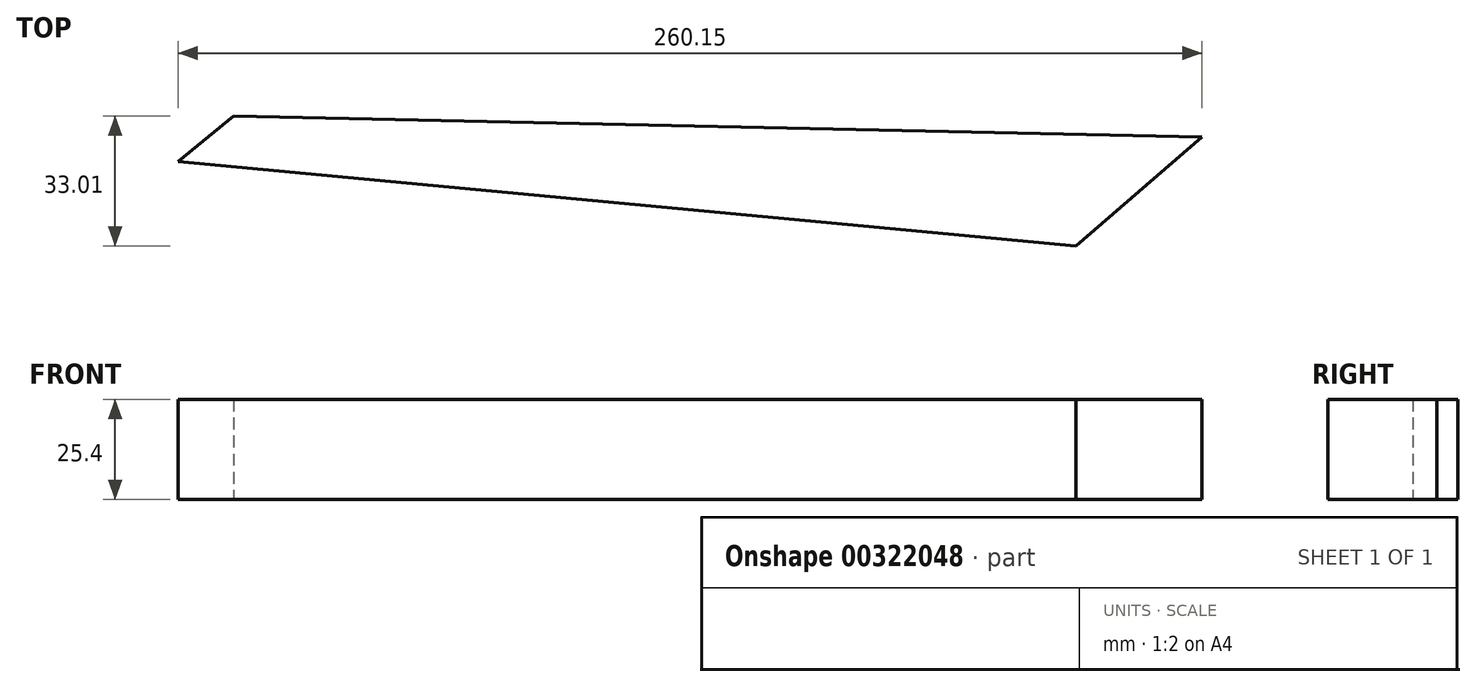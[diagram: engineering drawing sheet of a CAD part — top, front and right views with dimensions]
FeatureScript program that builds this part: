
annotation { "Feature Type Name" : "Feature", "Feature Type Description" : "" }
export const myFeature = defineFeature(function(context is Context, id is Id, definition is map)
    precondition{}
    {
        {
            var Q0;
            Q0=qCreatedBy(makeId("Top.planeOp"),FACE);
            var sketch = newSketch(context, id + "F0", { "sketchPlane" : qUnion([Q0])});
            skLineSegment(sketch, "E0", {"start": v(91.5, -86.95) * mm, "end": v(-136.55, -65.48) * mm});
            skLineSegment(sketch, "E1", {"start": v(-137.64, -66.37) * mm, "end": v(-122.43, -53.94) * mm});
            skLineSegment(sketch, "E2", {"start": v(-122.43, -53.94) * mm, "end": v(123.6, -59.33) * mm});
            skLineSegment(sketch, "E3", {"start": v(123.6, -59.33) * mm, "end": v(91.5, -86.95) * mm});
            skLineSegment(sketch, "E4", {"start": v(-122.43, -53.94) * mm, "end": v(-93.65, -30.42) * mm});
            skLineSegment(sketch, "E5", {"start": v(-93.65, -30.42) * mm, "end": v(-48.37, -35.27) * mm});
            skLineSegment(sketch, "E6", {"start": v(-48.37, -35.27) * mm, "end": v(-71.22, -53.94) * mm});
            skSolve(sketch);
        }
        {
            var Q0;
            Q0 = qSketchRegion(id + "F0", true);
            extrude(context, id + "F1", {"entities" : qUnion([Q0]), "depth" : 25.4 * mm});
        }
    });
